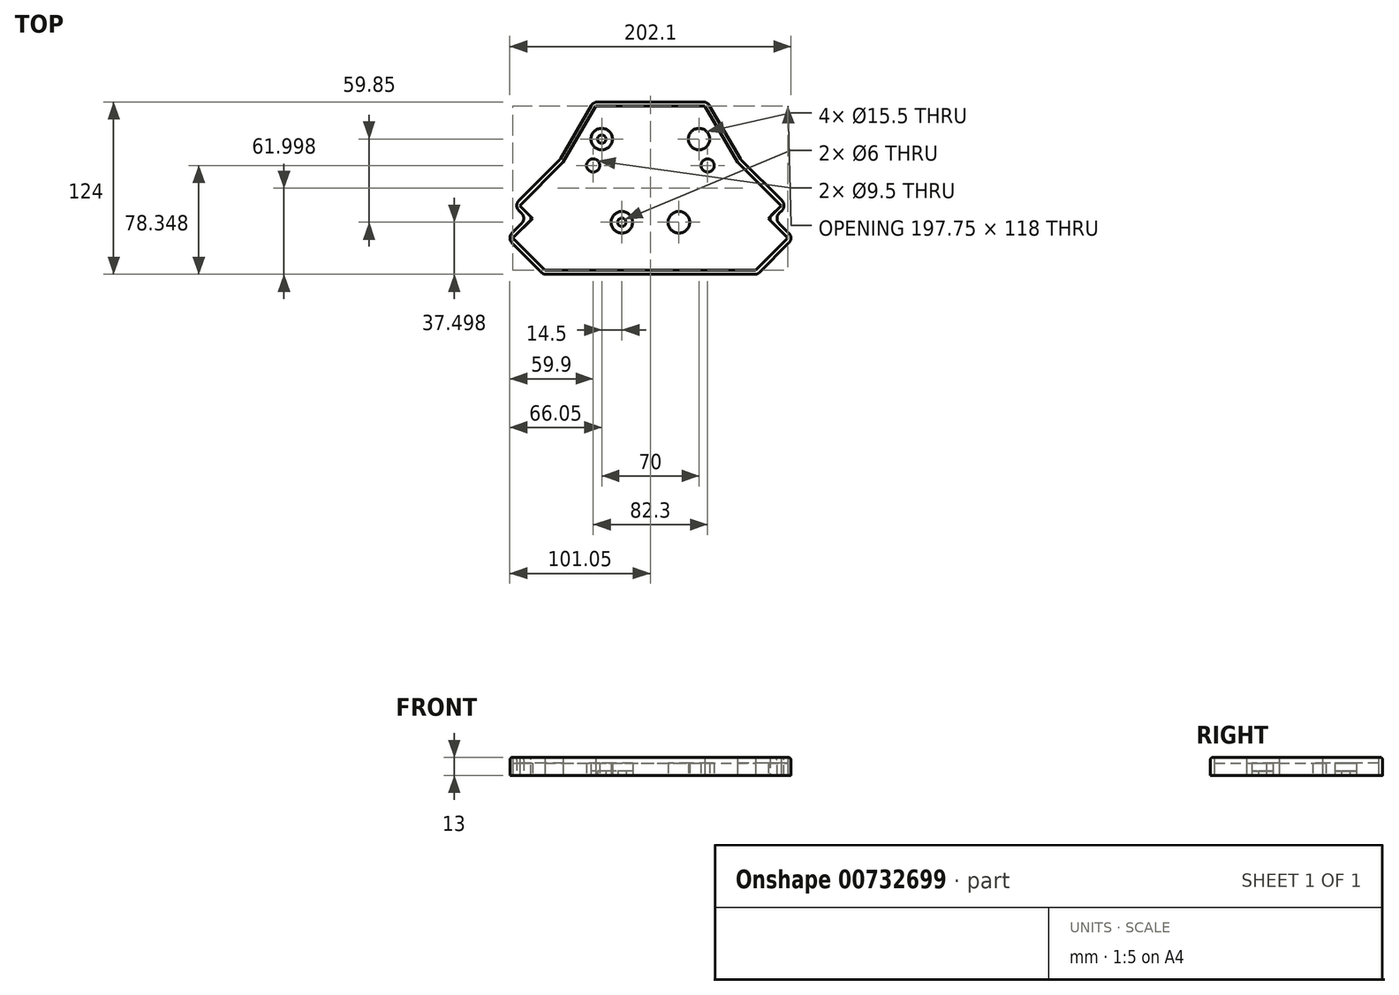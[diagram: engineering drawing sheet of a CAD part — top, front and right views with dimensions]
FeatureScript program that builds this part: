
annotation { "Feature Type Name" : "Feature", "Feature Type Description" : "" }
export const myFeature = defineFeature(function(context is Context, id is Id, definition is map)
    precondition{}
    {
        {
            var Q0;
            Q0=qCreatedBy(makeId("Top.planeOp"),FACE);
            var sketch = newSketch(context, id + "F0", { "sketchPlane" : qUnion([Q0])});
            skCircle(sketch, "E0", {"center": v(-35, 27.13) * mm, "radius": 7.75 * mm});
            skLineSegment(sketch, "E1", {"start": v(-35, 27.13) * mm, "end": v(0, 27.13) * mm, "construction": true});
            skLineSegment(sketch, "E2", {"start": v(0, 27.13) * mm, "end": v(0, 8.13) * mm, "construction": true});
            skLineSegment(sketch, "E3", {"start": v(0, 8.13) * mm, "end": v(-41.15, 8.13) * mm, "construction": true});
            skCircle(sketch, "E4", {"center": v(-41.15, 8.13) * mm, "radius": 4.75 * mm});
            skLineSegment(sketch, "E5", {"start": v(0, 27.13) * mm, "end": v(0, -32.72) * mm});
            skPoint(sketch, "E5.endSnap0", {"position": v(0, 17.63) * mm});
            skLineSegment(sketch, "E6", {"start": v(0, -32.72) * mm, "end": v(-20.5, -32.72) * mm, "construction": true});
            skCircle(sketch, "E7", {"center": v(-20.5, -32.72) * mm, "radius": 7.75 * mm});
            skCircle(sketch, "E8.MirrorC", {"center": v(20.5, -32.72) * mm, "radius": 7.75 * mm});
            skCircle(sketch, "E9.MirrorC", {"center": v(41.15, 8.13) * mm, "radius": 4.75 * mm});
            skCircle(sketch, "E10.MirrorC", {"center": v(35, 27.13) * mm, "radius": 7.75 * mm});
            skLineSegment(sketch, "E11", {"start": v(35, 27.13) * mm, "end": v(35, 55.63) * mm, "construction": true});
            skLineSegment(sketch, "E12", {"start": v(72.6, 55.63) * mm, "end": v(-68.52, 55.63) * mm, "construction": true});
            skLineSegment(sketch, "E13", {"start": v(20.5, -32.72) * mm, "end": v(20.5, -70.22) * mm, "construction": true});
            skLineSegment(sketch, "E14", {"start": v(74.92, -70.22) * mm, "end": v(-74.89, -70.22) * mm, "construction": true});
            skCircle(sketch, "E15", {"center": v(-35, 27.13) * mm, "radius": 3 * mm});
            skCircle(sketch, "E16", {"center": v(-20.5, -32.72) * mm, "radius": 3 * mm});
            skCircle(sketch, "E17.MirrorC", {"center": v(20.5, -32.72) * mm, "radius": 3 * mm});
            skCircle(sketch, "E18.MirrorC", {"center": v(35, 27.13) * mm, "radius": 3 * mm});
            skSolve(sketch);
        }
        {
            var Q0;
            Q0=qCreatedBy(makeId("Top.planeOp"),FACE);
            var sketch = newSketch(context, id + "F1", { "sketchPlane" : qUnion([Q0])});
            skLineSegment(sketch, "E19.bottom", {"start": v(-91.1, -20.72) * mm, "end": v(-51.5, 18.87) * mm});
            skLineSegment(sketch, "E19.top", {"start": v(-41.6, -70.22) * mm, "end": v(-2, -30.62) * mm});
            skLineSegment(sketch, "E19.left", {"start": v(-91.1, -20.72) * mm, "end": v(-41.6, -70.22) * mm});
            skLineSegment(sketch, "E19.right", {"start": v(-51.5, 18.87) * mm, "end": v(-2, -30.62) * mm});
            skLineSegment(sketch, "E20.MirrorCS", {"start": v(91.1, -20.72) * mm, "end": v(41.6, -70.22) * mm});
            skLineSegment(sketch, "E21.MirrorCS", {"start": v(91.1, -20.72) * mm, "end": v(51.5, 18.87) * mm});
            skLineSegment(sketch, "E22.MirrorCS", {"start": v(41.6, -70.22) * mm, "end": v(2, -30.62) * mm});
            skLineSegment(sketch, "E23.MirrorCS", {"start": v(51.5, 18.87) * mm, "end": v(2, -30.62) * mm});
            skLineSegment(sketch, "E24.bottom", {"start": v(-32, 45.33) * mm, "end": v(32, 45.33) * mm});
            skLineSegment(sketch, "E24.top", {"start": v(-32, 12.33) * mm, "end": v(32, 12.33) * mm});
            skLineSegment(sketch, "E24.left", {"start": v(-32, 45.33) * mm, "end": v(-32, 12.33) * mm});
            skLineSegment(sketch, "E24.right", {"start": v(32, 45.33) * mm, "end": v(32, 12.33) * mm});
            skLineSegment(sketch, "E25", {"start": v(-32, 12.33) * mm, "end": v(0, 12.33) * mm});
            skLineSegment(sketch, "E26", {"start": v(-25.2, 12.33) * mm, "end": v(-25.2, -3.17) * mm});
            skLineSegment(sketch, "E27", {"start": v(-25.2, -3.17) * mm, "end": v(14.8, -3.17) * mm});
            skLineSegment(sketch, "E28", {"start": v(14.8, -3.17) * mm, "end": v(14.8, 12.33) * mm});
            skLineSegment(sketch, "E29.bottom", {"start": v(-91.97, -49.54) * mm, "end": v(-74.3, -67.22) * mm});
            skLineSegment(sketch, "E29.top", {"start": v(-78.54, -36.1) * mm, "end": v(-60.86, -53.79) * mm});
            skLineSegment(sketch, "E29.left", {"start": v(-91.97, -49.54) * mm, "end": v(-78.54, -36.1) * mm});
            skLineSegment(sketch, "E29.right", {"start": v(-74.3, -67.22) * mm, "end": v(-60.86, -53.79) * mm});
            skLineSegment(sketch, "E30.MirrorCS", {"start": v(78.54, -36.1) * mm, "end": v(60.86, -53.79) * mm});
            skLineSegment(sketch, "E31.MirrorCS", {"start": v(91.97, -49.54) * mm, "end": v(78.54, -36.1) * mm});
            skLineSegment(sketch, "E32.MirrorCS", {"start": v(91.97, -49.54) * mm, "end": v(74.3, -67.22) * mm});
            skLineSegment(sketch, "E33.MirrorCS", {"start": v(74.3, -67.22) * mm, "end": v(60.86, -53.79) * mm});
            skSolve(sketch);
        }
        {
            var Q0;
            Q0=qCreatedBy(makeId("Top.planeOp"),FACE);
            var sketch = newSketch(context, id + "F2", { "sketchPlane" : qUnion([Q0])});
            skLineSegment(sketch, "E34", {"start": v(-40.97, 53.78) * mm, "end": v(0, 53.78) * mm});
            skLineSegment(sketch, "E35", {"start": v(-76.95, -70.22) * mm, "end": v(0, -70.22) * mm});
            skPoint(sketch, "E36.visualSharp", {"position": v(-103.12, -44.06) * mm});
            skPoint(sketch, "E37.visualSharp", {"position": v(-65.15, 12.3) * mm});
            skPoint(sketch, "E38.visualSharp", {"position": v(-41, 53.78) * mm});
            skPoint(sketch, "E39.visualSharp", {"position": v(-98.17, -20.72) * mm});
            skLineSegment(sketch, "E40", {"start": v(-98.17, -20.72) * mm, "end": v(-48.67, -70.22) * mm, "construction": true});
            skLineSegment(sketch, "E41", {"start": v(-103.12, -44.06) * mm, "end": v(-76.95, -70.22) * mm});
            skLineSegment(sketch, "E42", {"start": v(-103.12, -44.06) * mm, "end": v(-88.97, -29.92) * mm});
            skLineSegment(sketch, "E43", {"start": v(-88.97, -29.92) * mm, "end": v(-98.17, -20.72) * mm});
            skLineSegment(sketch, "E44", {"start": v(-98.17, -20.72) * mm, "end": v(-88.97, -29.92) * mm});
            skLineSegment(sketch, "E45", {"start": v(-98.17, -20.72) * mm, "end": v(-65.15, 12.3) * mm});
            skLineSegment(sketch, "E46", {"start": v(-41, 53.78) * mm, "end": v(-65.15, 12.3) * mm});
            skLineSegment(sketch, "E47", {"start": v(0, 53.78) * mm, "end": v(-40.97, 53.78) * mm});
            skLineSegment(sketch, "E48.MirrorCS", {"start": v(88.97, -29.92) * mm, "end": v(98.17, -20.72) * mm});
            skPoint(sketch, "E49.MirrorP", {"position": v(65.15, 12.3) * mm});
            skLineSegment(sketch, "E50.MirrorCS", {"start": v(40.97, 53.78) * mm, "end": v(0, 53.78) * mm});
            skLineSegment(sketch, "E51.MirrorCS", {"start": v(98.17, -20.72) * mm, "end": v(65.15, 12.3) * mm});
            skLineSegment(sketch, "E52.MirrorCS", {"start": v(103.12, -44.06) * mm, "end": v(76.95, -70.22) * mm});
            skPoint(sketch, "E53.MirrorP", {"position": v(103.12, -44.06) * mm});
            skLineSegment(sketch, "E54.MirrorCS", {"start": v(98.17, -20.72) * mm, "end": v(48.67, -70.22) * mm, "construction": true});
            skLineSegment(sketch, "E55.MirrorCS", {"start": v(76.95, -70.22) * mm, "end": v(0, -70.22) * mm});
            skLineSegment(sketch, "E56.MirrorCS", {"start": v(98.17, -20.72) * mm, "end": v(88.97, -29.92) * mm});
            skLineSegment(sketch, "E57.MirrorCS", {"start": v(41, 53.78) * mm, "end": v(65.15, 12.3) * mm});
            skPoint(sketch, "E58.MirrorP", {"position": v(98.17, -20.72) * mm});
            skPoint(sketch, "E59.MirrorP", {"position": v(41, 53.78) * mm});
            skLineSegment(sketch, "E60.MirrorCS", {"start": v(103.12, -44.06) * mm, "end": v(88.97, -29.92) * mm});
            skLineSegment(sketch, "E61.MirrorCS", {"start": v(0, 53.78) * mm, "end": v(40.97, 53.78) * mm});
            skCircle(sketch, "E62.0.0", {"center": v(-20.5, -32.72) * mm, "radius": 7.75 * mm});
            skCircle(sketch, "E62.1.0", {"center": v(20.5, -32.72) * mm, "radius": 7.75 * mm});
            skCircle(sketch, "E62.2.0", {"center": v(41.15, 8.13) * mm, "radius": 4.75 * mm});
            skCircle(sketch, "E62.3.0", {"center": v(35, 27.13) * mm, "radius": 7.75 * mm});
            skCircle(sketch, "E62.4.0", {"center": v(-41.15, 8.13) * mm, "radius": 4.75 * mm});
            skCircle(sketch, "E62.5.0", {"center": v(-35, 27.13) * mm, "radius": 7.75 * mm});
            skLineSegment(sketch, "E63", {"start": v(76.95, -70.22) * mm, "end": v(103.12, -44.06) * mm});
            skLineSegment(sketch, "E64", {"start": v(65.15, 12.3) * mm, "end": v(41, 53.78) * mm});
            skLineSegment(sketch, "E65", {"start": v(-40.97, 53.78) * mm, "end": v(-65.15, 12.3) * mm});
            skSolve(sketch);
        }
        {
            var Q0;
            Q0=qCreatedBy(makeId("Top.planeOp"),FACE);
            var sketch = newSketch(context, id + "F3", { "sketchPlane" : qUnion([Q0])});
            skPoint(sketch, "E66.0", {"position": v(-41, 53.78) * mm});
            skPoint(sketch, "E66.1", {"position": v(41, 53.78) * mm});
            skPoint(sketch, "E66.2", {"position": v(65.15, 12.3) * mm});
            skPoint(sketch, "E66.3", {"position": v(98.17, -20.72) * mm});
            skPoint(sketch, "E66.4", {"position": v(88.97, -29.92) * mm});
            skPoint(sketch, "E66.5", {"position": v(103.12, -44.06) * mm});
            skPoint(sketch, "E66.6", {"position": v(76.95, -70.22) * mm});
            skPoint(sketch, "E66.7", {"position": v(-76.95, -70.22) * mm});
            skPoint(sketch, "E66.8", {"position": v(-103.12, -44.06) * mm});
            skPoint(sketch, "E66.9", {"position": v(-88.97, -29.92) * mm});
            skPoint(sketch, "E66.10", {"position": v(-98.17, -20.72) * mm});
            skPoint(sketch, "E66.11", {"position": v(-65.15, 12.3) * mm});
            skLineSegment(sketch, "E67", {"start": v(-41, 53.78) * mm, "end": v(41, 53.78) * mm});
            skLineSegment(sketch, "E68", {"start": v(41, 53.78) * mm, "end": v(65.15, 12.3) * mm});
            skLineSegment(sketch, "E69", {"start": v(98.17, -20.72) * mm, "end": v(65.15, 12.3) * mm});
            skLineSegment(sketch, "E70", {"start": v(98.17, -20.72) * mm, "end": v(88.97, -29.92) * mm});
            skLineSegment(sketch, "E71", {"start": v(88.97, -29.92) * mm, "end": v(103.12, -44.06) * mm});
            skLineSegment(sketch, "E72", {"start": v(103.12, -44.06) * mm, "end": v(76.95, -70.22) * mm});
            skLineSegment(sketch, "E73", {"start": v(-76.95, -70.22) * mm, "end": v(76.95, -70.22) * mm});
            skLineSegment(sketch, "E74", {"start": v(-76.95, -70.22) * mm, "end": v(-103.12, -44.06) * mm});
            skLineSegment(sketch, "E75", {"start": v(-103.12, -44.06) * mm, "end": v(-88.97, -29.92) * mm});
            skLineSegment(sketch, "E76", {"start": v(-65.15, 12.3) * mm, "end": v(-98.17, -20.72) * mm});
            skLineSegment(sketch, "E77", {"start": v(-98.17, -20.72) * mm, "end": v(-88.97, -29.92) * mm});
            skLineSegment(sketch, "E78", {"start": v(-65.15, 12.3) * mm, "end": v(-41, 53.78) * mm});
            skLineSegment(sketch, "E79.0", {"start": v(-62.75, 10.45) * mm, "end": v(-39.28, 50.78) * mm});
            skLineSegment(sketch, "E79.1", {"start": v(84.73, -29.92) * mm, "end": v(98.87, -44.06) * mm});
            skLineSegment(sketch, "E79.2", {"start": v(93.92, -20.72) * mm, "end": v(84.73, -29.92) * mm});
            skLineSegment(sketch, "E79.3", {"start": v(93.92, -20.72) * mm, "end": v(62.75, 10.45) * mm});
            skLineSegment(sketch, "E79.4", {"start": v(39.28, 50.78) * mm, "end": v(62.75, 10.45) * mm});
            skLineSegment(sketch, "E79.5", {"start": v(98.87, -44.06) * mm, "end": v(75.71, -67.22) * mm});
            skLineSegment(sketch, "E79.6", {"start": v(-39.28, 50.78) * mm, "end": v(39.28, 50.78) * mm});
            skLineSegment(sketch, "E79.7", {"start": v(-75.71, -67.22) * mm, "end": v(75.71, -67.22) * mm});
            skLineSegment(sketch, "E79.8", {"start": v(-75.71, -67.22) * mm, "end": v(-98.87, -44.06) * mm});
            skLineSegment(sketch, "E79.9", {"start": v(-98.87, -44.06) * mm, "end": v(-84.73, -29.92) * mm});
            skLineSegment(sketch, "E79.10", {"start": v(-93.92, -20.72) * mm, "end": v(-84.73, -29.92) * mm});
            skLineSegment(sketch, "E79.11", {"start": v(-62.75, 10.45) * mm, "end": v(-93.92, -20.72) * mm});
            skCircle(sketch, "E80.0", {"center": v(35, 27.13) * mm, "radius": 7.75 * mm});
            skCircle(sketch, "E80.1", {"center": v(41.15, 8.13) * mm, "radius": 4.75 * mm});
            skCircle(sketch, "E80.2", {"center": v(-41.15, 8.13) * mm, "radius": 4.75 * mm});
            skCircle(sketch, "E80.3", {"center": v(-20.5, -32.72) * mm, "radius": 7.75 * mm});
            skCircle(sketch, "E80.4", {"center": v(20.5, -32.72) * mm, "radius": 7.75 * mm});
            skCircle(sketch, "E80.5", {"center": v(-35, 27.13) * mm, "radius": 7.75 * mm});
            skCircle(sketch, "E81.0", {"center": v(-35, 27.13) * mm, "radius": 3 * mm});
            skCircle(sketch, "E81.1", {"center": v(35, 27.13) * mm, "radius": 3 * mm});
            skCircle(sketch, "E81.2", {"center": v(-20.5, -32.72) * mm, "radius": 3 * mm});
            skCircle(sketch, "E81.3", {"center": v(20.5, -32.72) * mm, "radius": 3 * mm});
            skSolve(sketch);
        }
        {
            var Q0;
            Q0=makeQuery(id+"F3.imprint","IMPRINT",FACE,{"disambiguationData":[TD([[makeQuery(id+"F3.imprint","IMPRINT",EDGE,{"derivedFrom":sQuery(id+"F3.wireOp",EDGE,"E67")}),-1.0]])]});
            extrude(context, id + "F4", {"entities" : qUnion([Q0]), "depth" : 13 * mm, "offsetDistance" : 25 * mm});
        }
        {
            var Q0;
            Q0=makeQuery(id+"F0.imprint","IMPRINT",FACE,{"disambiguationData":[TD([[makeQuery(id+"F0.imprint","IMPRINT",EDGE,{"derivedFrom":sQuery(id+"F0.wireOp",EDGE,"E0")}),1.0]])]});
            var Q1;
            Q1=makeQuery(id+"F0.imprint","IMPRINT",FACE,{"disambiguationData":[TD([[makeQuery(id+"F0.imprint","IMPRINT",EDGE,{"derivedFrom":sQuery(id+"F0.wireOp",EDGE,"E10.MirrorC")}),-1.0]])]});
            var Q2;
            Q2=makeQuery(id+"F0.imprint","IMPRINT",FACE,{"disambiguationData":[TD([[makeQuery(id+"F0.imprint","IMPRINT",EDGE,{"derivedFrom":sQuery(id+"F0.wireOp",EDGE,"E8.MirrorC")}),-1.0]])]});
            var Q3;
            Q3=makeQuery(id+"F0.imprint","IMPRINT",FACE,{"disambiguationData":[TD([[makeQuery(id+"F0.imprint","IMPRINT",EDGE,{"derivedFrom":sQuery(id+"F0.wireOp",EDGE,"E7")}),1.0]])]});
            extrude(context, id + "F5", {"entities" : qUnion([Q0, Q1, Q2, Q3]), "depth" : 3 * mm, "offsetDistance" : 25 * mm});
        }
        {
            var Q0;
            Q0=makeQuery(id+"F3.imprint","IMPRINT",FACE,{"disambiguationData":[TD([[makeQuery(id+"F3.imprint","IMPRINT",EDGE,{"derivedFrom":sQuery(id+"F3.wireOp",EDGE,"E79.0")}),-1.0]])]});
            extrude(context, id + "F6", {"entities" : qUnion([Q0]), "depth" : 9 * mm, "offsetDistance" : 25 * mm});
        }
        {
            var Q0;
            Q0=makeQuery(id+"F4.opExtrude","SWEPT_EDGE",EDGE,{"disambiguationData":[OSD([sQuery(id+"F3.wireOp",EDGE,"E69"),sQuery(id+"F3.wireOp",EDGE,"E70")])]});
            var Q1;
            Q1=makeQuery(id+"F4.opExtrude","SWEPT_EDGE",EDGE,{"disambiguationData":[OSD([sQuery(id+"F3.wireOp",EDGE,"E71"),sQuery(id+"F3.wireOp",EDGE,"E72")])]});
            var Q2;
            Q2=makeQuery(id+"F4.opExtrude","SWEPT_EDGE",EDGE,{"disambiguationData":[OSD([sQuery(id+"F3.wireOp",EDGE,"E72"),sQuery(id+"F3.wireOp",EDGE,"E73")])]});
            var Q3;
            Q3=makeQuery(id+"F4.opExtrude","SWEPT_EDGE",EDGE,{"disambiguationData":[OSD([sQuery(id+"F3.wireOp",EDGE,"E73"),sQuery(id+"F3.wireOp",EDGE,"E74")])]});
            var Q4;
            Q4=makeQuery(id+"F4.opExtrude","SWEPT_EDGE",EDGE,{"disambiguationData":[OSD([sQuery(id+"F3.wireOp",EDGE,"E74"),sQuery(id+"F3.wireOp",EDGE,"E75")])]});
            var Q5;
            Q5=makeQuery(id+"F4.opExtrude","SWEPT_EDGE",EDGE,{"disambiguationData":[OSD([sQuery(id+"F3.wireOp",EDGE,"E76"),sQuery(id+"F3.wireOp",EDGE,"E77")])]});
            var Q6;
            Q6=makeQuery(id+"F4.opExtrude","SWEPT_EDGE",EDGE,{"disambiguationData":[OSD([sQuery(id+"F3.wireOp",EDGE,"E75"),sQuery(id+"F3.wireOp",EDGE,"E77")])]});
            var Q7;
            Q7=makeQuery(id+"F4.opExtrude","SWEPT_EDGE",EDGE,{"disambiguationData":[OSD([sQuery(id+"F3.wireOp",EDGE,"E76"),sQuery(id+"F3.wireOp",EDGE,"E78")])]});
            var Q8;
            Q8=makeQuery(id+"F4.opExtrude","SWEPT_EDGE",EDGE,{"disambiguationData":[OSD([sQuery(id+"F3.wireOp",EDGE,"E67"),sQuery(id+"F3.wireOp",EDGE,"E78")])]});
            var Q9;
            Q9=makeQuery(id+"F4.opExtrude","SWEPT_EDGE",EDGE,{"disambiguationData":[OSD([sQuery(id+"F3.wireOp",EDGE,"E67"),sQuery(id+"F3.wireOp",EDGE,"E68")])]});
            var Q10;
            Q10=makeQuery(id+"F4.opExtrude","SWEPT_EDGE",EDGE,{"disambiguationData":[OSD([sQuery(id+"F3.wireOp",EDGE,"E68"),sQuery(id+"F3.wireOp",EDGE,"E69")])]});
            var Q11;
            Q11=makeQuery(id+"F4.opExtrude","SWEPT_EDGE",EDGE,{"disambiguationData":[OSD([sQuery(id+"F3.wireOp",EDGE,"E70"),sQuery(id+"F3.wireOp",EDGE,"E71")])]});
            fillet(context, id + "F7", {"entities" : qUnion([Q0, Q1, Q2, Q3, Q4, Q5, Q6, Q7, Q8, Q9, Q10, Q11]), "radius" : 5 * mm, "tangentPropagation" : true, "allowEdgeOverflow" : false});
        }
        {
            var Q0;
            Q0=makeQuery(id+"F4.opExtrude","CAP_EDGE",EDGE,{"disambiguationData":[OSD([sQuery(id+"F3.wireOp",EDGE,"E73")])],"isStart":false});
            fillet(context, id + "F8", {"entities" : qUnion([Q0]), "radius" : 2 * mm, "tangentPropagation" : true, "allowEdgeOverflow" : false});
        }
        {
            var Q0;
            Q0=makeQuery(id+"F4.opExtrude","SWEPT_EDGE",EDGE,{"disambiguationData":[OSD([sQuery(id+"F3.wireOp",EDGE,"E79.1"),sQuery(id+"F3.wireOp",EDGE,"E79.2")])]});
            var Q1;
            Q1=makeQuery(id+"F4.opExtrude","SWEPT_EDGE",EDGE,{"disambiguationData":[OSD([sQuery(id+"F3.wireOp",EDGE,"E79.9"),sQuery(id+"F3.wireOp",EDGE,"E79.10")])]});
            fillet(context, id + "F9", {"entities" : qUnion([Q0, Q1]), "radius" : 3 * mm, "tangentPropagation" : true, "allowEdgeOverflow" : false});
        }
    });
